# Revit family: Commercial Peened Wall Mount Grab bar C9061 seris
name_source: partatom
category: Plumbing Fixtures
revit_build: Autodesk Revit 2018 (Build: 20181015_0930(x64)
units: mm (PartAtom-declared; Revit-internal decimal feet)

## family parameters
Always vertical = Yes
Cut with Voids When Loaded = No
Part Type = Normal
Room Calculation Point = No
Round Connector Dimension = Use Diameter
Shared = No
Work Plane-Based = No

## types (6) — shared parameters
URL = https://kromedispense.co.in

## per-type parameters (varying)
| type | Grab Bar Length | Model | Weight (lbs) |
| C9061-9" Commercial Peened Wall Mount Grab Bars | 0' - 9" | C9061 | .97 |
| C9062-12" Commercial Peened Wall Mount Grab Bars | 1' - 0" | C9062 | 1.13 |
| C9065-36" Commercial Peened Wall Mount Grab Bars | 3' - 0" | C9065 | 2.37 |
| C9063-18" Commercial Peened Wall Mount Grab Bars | 1' - 6" | C9063 | 1.44 |
| C9066-48" Commercial Peened Wall Mount Grab Bars | 4' - 0" | C9066 | 2.99 |
| C9064-24" Commercial Peened Wall Mount Grab Bars | 2' - 0" | C9064 | 1.75 |

## geometry (parser evidence)
native form markers: Sweep x3
no freeform markers — native parametric forms only
